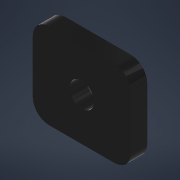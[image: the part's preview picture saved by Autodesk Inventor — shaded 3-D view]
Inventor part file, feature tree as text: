
AUTODESK INVENTOR PART (.ipt)
format: ipt  version: 2021 (Build 250183000, 183)  size: 109,056 bytes
history: native  units: mm
features: other x5, reference x2, extrude x1
ambient origin geometry x8: Origin, YZ Plane, XZ Plane, XY Plane, X Axis, Y Axis, Z Axis, Center Point
bodies: Solid1 (feature_tree)
feature tree (8):
  extrude  "washer"  Depth=10.471521mm
  other  "washer_sketch"
  reference  "Reference1"
  reference  "Reference2"
  other  "<userpath>\Documents\Dev\tco-cad\camera_mount\assembly_camera_mount.iam"
  other  "assembly_camera_mount.iam"
  other  "linear_stepper_base:1"
  other  "mount_linear_stepper:1"
